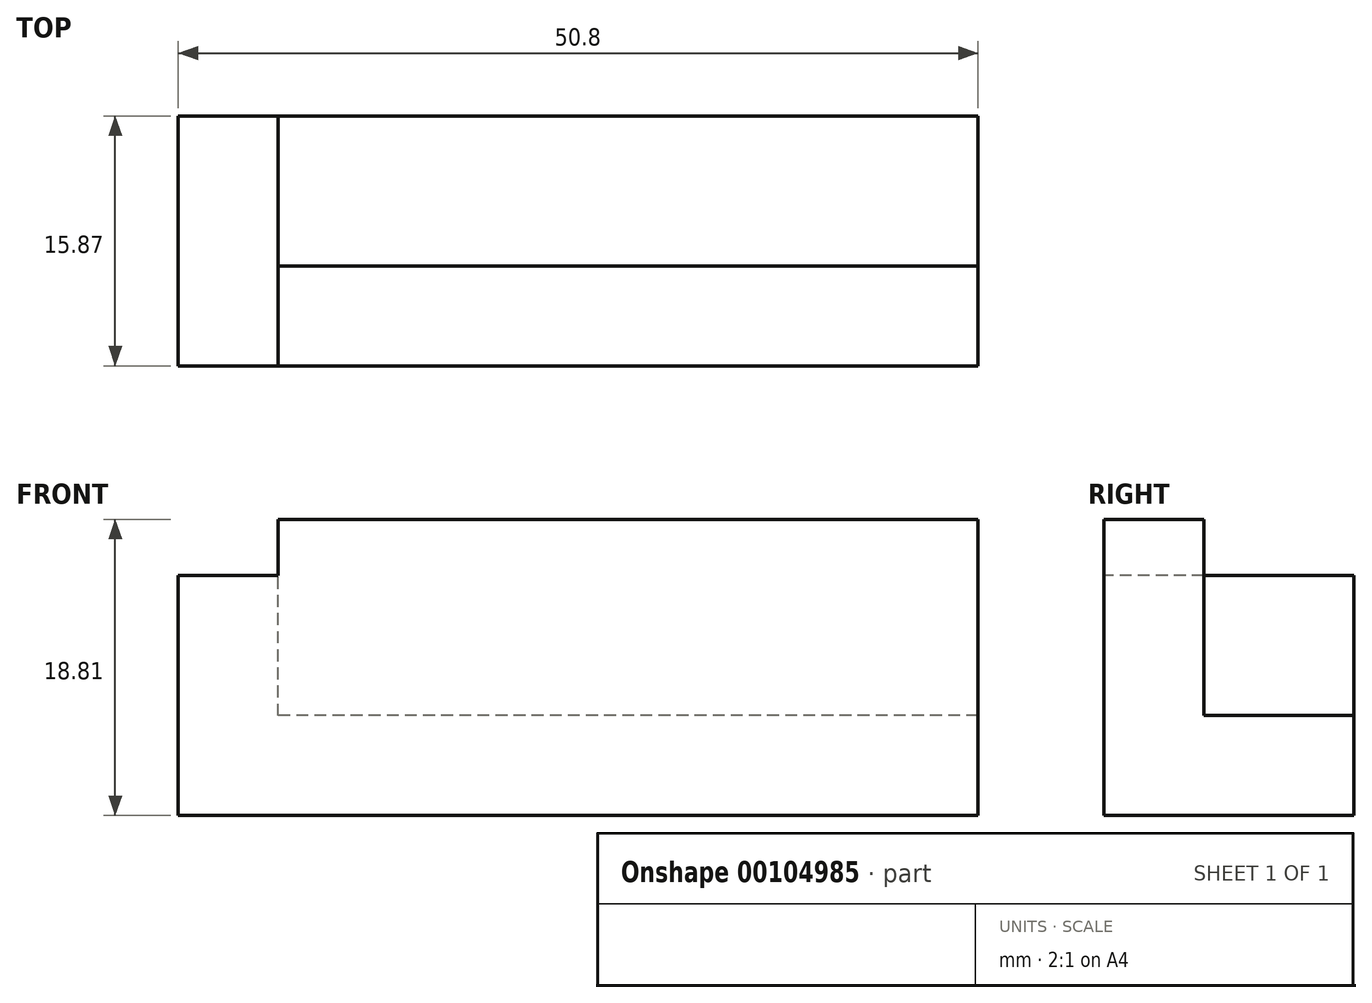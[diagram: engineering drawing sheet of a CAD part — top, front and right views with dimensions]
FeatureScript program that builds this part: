
annotation { "Feature Type Name" : "Feature", "Feature Type Description" : "" }
export const myFeature = defineFeature(function(context is Context, id is Id, definition is map)
    precondition{}
    {
        {
            var Q0;
            Q0=qCreatedBy(makeId("Top.planeOp"),FACE);
            var sketch = newSketch(context, id + "F0", { "sketchPlane" : qUnion([Q0])});
            skLineSegment(sketch, "E0.bottom", {"start": v(6.35, 0) * mm, "end": v(50.8, 0) * mm});
            skLineSegment(sketch, "E0.right", {"start": v(50.8, 0) * mm, "end": v(50.8, 6.35) * mm});
            skLineSegment(sketch, "E1.right", {"start": v(6.35, 0) * mm, "end": v(6.35, 6.35) * mm});
            skLineSegment(sketch, "E2.top", {"start": v(6.35, 6.35) * mm, "end": v(50.8, 6.35) * mm});
            skLineSegment(sketch, "E3.bottom", {"start": v(0, 0) * mm, "end": v(50.8, 0) * mm});
            skLineSegment(sketch, "E3.top", {"start": v(0, 12.7) * mm, "end": v(50.8, 12.7) * mm});
            skLineSegment(sketch, "E3.left", {"start": v(0, 0) * mm, "end": v(0, 12.7) * mm});
            skLineSegment(sketch, "E3.right", {"start": v(50.8, 0) * mm, "end": v(50.8, 12.7) * mm});
            skLineSegment(sketch, "E4", {"start": v(6.35, 6.35) * mm, "end": v(6.35, 12.7) * mm});
            skSolve(sketch);
        }
        {
            var Q0;
            Q0=qCreatedBy(makeId("Front.planeOp"),FACE);
            var sketch = newSketch(context, id + "F1", { "sketchPlane" : qUnion([Q0])});
            skLineSegment(sketch, "E5.bottom", {"start": v(0, 0) * mm, "end": v(50.8, 0) * mm});
            skLineSegment(sketch, "E5.top", {"start": v(0, 15.24) * mm, "end": v(6.35, 15.24) * mm});
            skLineSegment(sketch, "E5.left", {"start": v(0, 0) * mm, "end": v(0, 15.24) * mm});
            skLineSegment(sketch, "E5.right", {"start": v(50.8, 0) * mm, "end": v(50.8, 18.8) * mm});
            skLineSegment(sketch, "E6.bottom", {"start": v(50.8, 18.8) * mm, "end": v(6.35, 18.8) * mm});
            skLineSegment(sketch, "E6.left", {"start": v(50.8, 18.8) * mm, "end": v(50.8, 6.1) * mm});
            skLineSegment(sketch, "E7", {"start": v(6.35, 15.24) * mm, "end": v(6.35, 18.8) * mm});
            skSolve(sketch);
        }
        {
            var Q0;
            Q0 = qSketchRegion(id + "F1", true);
            extrude(context, id + "F2", {"entities" : qUnion([Q0]), "endBound" : BoundingType.SYMMETRIC, "oppositeDirection" : true, "depth" : 6.35 * mm});
        }
        {
            var Q0;
            Q0=qCreatedBy(makeId("Right.planeOp"),FACE);
            var sketch = newSketch(context, id + "F3", { "sketchPlane" : qUnion([Q0])});
            skLineSegment(sketch, "E8.bottom", {"start": v(0, 0) * mm, "end": v(12.7, 0) * mm});
            skLineSegment(sketch, "E8.top", {"start": v(0, 15.24) * mm, "end": v(12.7, 15.24) * mm});
            skLineSegment(sketch, "E8.left", {"start": v(0, 0) * mm, "end": v(0, 15.24) * mm});
            skLineSegment(sketch, "E8.right", {"start": v(12.7, 0) * mm, "end": v(12.7, 15.24) * mm});
            skLineSegment(sketch, "E9.bottom", {"start": v(12.7, 0) * mm, "end": v(0, 0) * mm});
            skLineSegment(sketch, "E9.top", {"start": v(12.7, 15.24) * mm, "end": v(0, 15.24) * mm});
            skLineSegment(sketch, "E9.right", {"start": v(0, 15.24) * mm, "end": v(0, 15.24) * mm});
            skPoint(sketch, "E10.orphan", {"position": v(0, 15.24) * mm});
            skSolve(sketch);
        }
        {
            var Q0;
            Q0 = qSketchRegion(id + "F0", true);
            var Q1;
            Q1=makeQuery(id+"F2.opExtrude","SWEPT_FACE",FACE,{"disambiguationData":[OSD([sQuery(id+"F1.wireOp",EDGE,"E6.bottom")])]});
            extrude(context, id + "F4", {"entities" : qUnion([Q0]), "operationType" : NewBodyOperationType.ADD, "endBoundEntityFace" : qUnion([Q1]), "depth" : 6.35 * mm});
        }
        {
            var Q0;
            Q0 = qSketchRegion(id + "F3", true);
            extrude(context, id + "F5", {"entities" : qUnion([Q0]), "operationType" : NewBodyOperationType.ADD, "depth" : 6.35 * mm});
        }
    });
